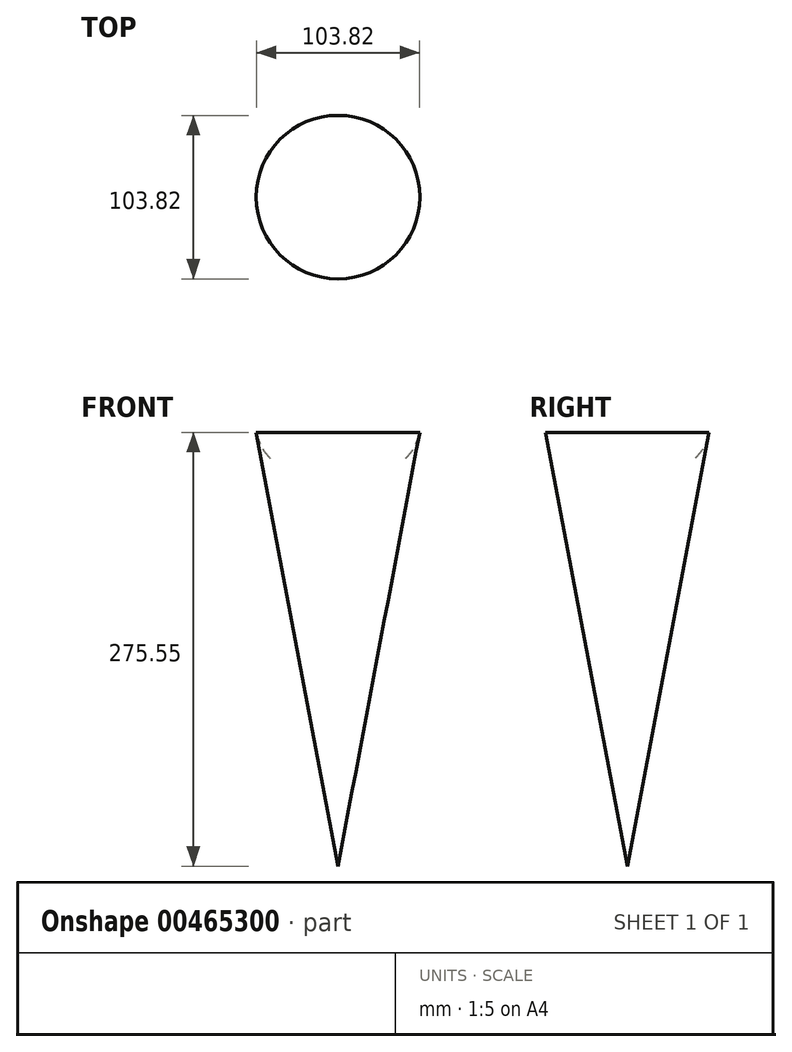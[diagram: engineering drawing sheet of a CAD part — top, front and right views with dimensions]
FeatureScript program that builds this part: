
annotation { "Feature Type Name" : "Feature", "Feature Type Description" : "" }
export const myFeature = defineFeature(function(context is Context, id is Id, definition is map)
    precondition{}
    {
        {
            var Q0;
            Q0=qCreatedBy(makeId("Front.planeOp"),FACE);
            var sketch = newSketch(context, id + "F0", { "sketchPlane" : qUnion([Q0])});
            skArc(sketch, "E0", {"start": v(0, 28.12) * mm, "mid": v(-36.21, 33) * mm, "end": v(-51.91, 0) * mm});
            skLineSegment(sketch, "E1", {"start": v(-51.91, 0) * mm, "end": v(0, -275.55) * mm});
            skLineSegment(sketch, "E2", {"start": v(0, 28.12) * mm, "end": v(0, -275.55) * mm});
            skSolve(sketch);
        }
        {
            var Q0;
            Q0 = qSketchRegion(id + "F0", true);
            var Q1;
            Q1=sQuery(id+"F0.wireOp",EDGE,"E2");
            revolve(context, id + "F1", {"entities" : qUnion([Q0]), "axis" : qUnion([Q1]), "revolveType" : RevolveType.FULL});
        }
    });
